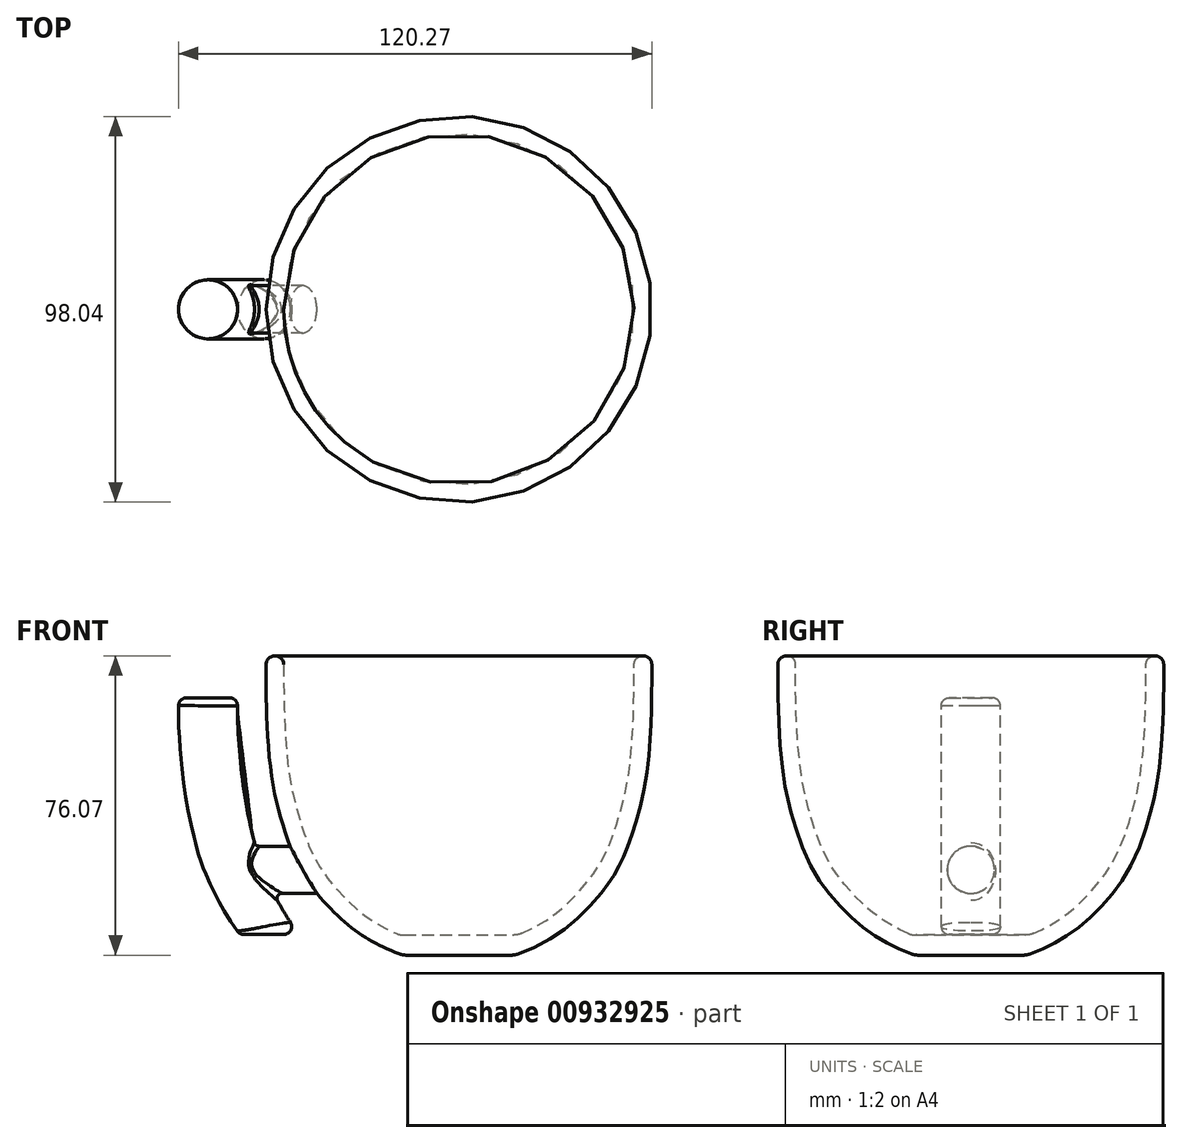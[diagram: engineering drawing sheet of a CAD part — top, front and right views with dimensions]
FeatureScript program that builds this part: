
annotation { "Feature Type Name" : "Feature", "Feature Type Description" : "" }
export const myFeature = defineFeature(function(context is Context, id is Id, definition is map)
    precondition{}
    {
        {
            var Q0;
            Q0=qCreatedBy(makeId("Front.planeOp"),FACE);
            var sketch = newSketch(context, id + "F0", { "sketchPlane" : qUnion([Q0])});
            skLineSegment(sketch, "E0", {"start": v(0, 78.82) * mm, "end": v(-49, 78.82) * mm});
            skLineSegment(sketch, "E1", {"start": v(0, 0) * mm, "end": v(0, 78.82) * mm});
            skFitSpline(sketch, "E2", {"points": [v(-49, 78.82) * mm, v(-49, 71.2) * mm, v(-47.95, 50.94) * mm, v(-44.24, 34.32) * mm, v(-38.54, 21.8) * mm, v(-27.37, 9.77) * mm, v(-17.3, 3.96) * mm, v(0, 0) * mm], "startDerivative": vector(-0.53, -120.05) * mm, "endDerivative": vector(126.32, 0) * mm});
            skSolve(sketch);
        }
        {
            var Q0;
            Q0=qSketchRegion(id+"F0",true);
            var Q1;
            Q1=sQuery(id+"F0.wireOp",EDGE,"E1");
            revolve(context, id + "F1", {"surfaceOperationType" : NewSurfaceOperationType.NEW, "entities" : qUnion([Q0]), "axis" : qUnion([Q1]), "revolveType" : RevolveType.FULL});
        }
        {
            var Q0;
            Q0=makeQuery(id+"F1.opRevolve","SWEPT_FACE",FACE,{"disambiguationData":[OSD([sQuery(id+"F0.wireOp",EDGE,"E0")])]});
            shell(context, id + "F2", {"entities" : qUnion([Q0]), "thickness" : 4.5 * mm});
        }
        {
            var Q0;
            Q0=makeQuery(id+"F1.opRevolve","SWEPT_EDGE",EDGE,{"disambiguationData":[OSD([sQuery(id+"F0.wireOp",EDGE,"E0"),sQuery(id+"F0.wireOp",EDGE,"E2")])]});
            var Q1;
            Q1=makeQuery(id+"F2.opShell","OFFSET_EDGE",EDGE,{"disambiguationData":[OSD([sQuery(id+"F0.wireOp",EDGE,"E0"),sQuery(id+"F0.wireOp",EDGE,"E2")])]});
            fillet(context, id + "F3", {"entities" : qUnion([Q0, Q1]), "radius" : 2.25 * mm, "tangentPropagation" : true, "defaultsChanged" : true, "vertexSettings" : [], "allowEdgeOverflow" : false});
        }
        {
            var Q0;
            Q0=qCreatedBy(makeId("Front.planeOp"),FACE);
            var sketch = newSketch(context, id + "F4", { "sketchPlane" : qUnion([Q0])});
            skLineSegment(sketch, "E3", {"start": v(-41.77, 30.38) * mm, "end": v(-53.43, 30.38) * mm});
            skLineSegment(sketch, "E4", {"start": v(-49.23, 20.12) * mm, "end": v(-36.53, 20.12) * mm});
            skLineSegment(sketch, "E5", {"start": v(-36.53, 20.12) * mm, "end": v(-41.77, 30.38) * mm});
            skFitSpline(sketch, "E6", {"points": [v(-42.03, 8) * mm, v(-47.44, 16.94) * mm, v(-49.23, 20.12) * mm, v(-51.33, 24.44) * mm, v(-53.43, 30.38) * mm, v(-55.23, 38.72) * mm, v(-56.67, 49.18) * mm, v(-57.32, 61.86) * mm, v(-57.58, 68.13) * mm, v(-57.6, 68.09) * mm], "startDerivative": vector(-47.1, 69.03) * mm, "endDerivative": vector(-6.03, -13.35) * mm});
            skLineSegment(sketch, "E7", {"start": v(-57.58, 68.13) * mm, "end": v(-69.83, 68.13) * mm});
            skFitSpline(sketch, "E8", {"points": [v(-69.83, 68.13) * mm, v(-69.83, 61.07) * mm, v(-69.06, 51.29) * mm, v(-67.63, 40.46) * mm, v(-65.54, 31.18) * mm, v(-63.64, 25) * mm, v(-58.64, 14.66) * mm, v(-54.3, 8) * mm], "startDerivative": vector(-1.12, -53.42) * mm, "endDerivative": vector(31.44, -44.67) * mm});
            skLineSegment(sketch, "E9", {"start": v(-54.3, 8) * mm, "end": v(-42.03, 8) * mm});
            skSolve(sketch);
        }
        {
            var Q0;
            Q0=qCreatedBy(makeId("Right.planeOp"),FACE);
            cPlane(context, id + "F5", {"entities" : qUnion([Q0]), "cplaneType" : CPlaneType.OFFSET, "offset" : 55 * mm, "oppositeDirection" : true, "width" : 150 * mm, "height" : 150 * mm});
        }
        {
            var Q0;
            Q0=qCreatedBy(id+"F5.planeOp",FACE);
            var sketch = newSketch(context, id + "F6", { "sketchPlane" : qUnion([Q0])});
            skPoint(sketch, "E10.middle", {"position": v(0, 24.44) * mm});
            skCircle(sketch, "E11", {"center": v(0, 24.44) * mm, "radius": 6 * mm});
            skSolve(sketch);
        }
        {
            var Q0;
            Q0=qSketchRegion(id+"F6",true);
            extrude(context, id + "F7", {"entities" : qUnion([Q0]), "operationType" : NewBodyOperationType.ADD, "endBound" : BoundingType.UP_TO_NEXT, "depth" : 25 * mm, "offsetDistance" : 25 * mm});
        }
        {
            var Q0;
            Q0=qCreatedBy(makeId("Top.planeOp"),FACE);
            cPlane(context, id + "F8", {"entities" : qUnion([Q0]), "cplaneType" : CPlaneType.OFFSET, "offset" : 8 * mm, "width" : 150 * mm, "height" : 150 * mm});
        }
        {
            var Q0;
            Q0=qCreatedBy(id+"F8.planeOp",FACE);
            var sketch = newSketch(context, id + "F9", { "sketchPlane" : qUnion([Q0])});
            skPoint(sketch, "E12.middle", {"position": v(-48.17, 0) * mm});
            skCircle(sketch, "E13", {"center": v(-48.17, 0) * mm, "radius": 7.5 * mm});
            skSolve(sketch);
        }
        {
            var Q0;
            Q0=qSketchRegion(id+"F9",true);
            var Q1;
            Q1=sQuery(id+"F4.wireOp",EDGE,"E8");
            sweep(context, id + "F10", {"operationType" : NewBodyOperationType.ADD, "profiles" : qUnion([Q0]), "path" : qUnion([Q1]), "keepProfileOrientation" : true});
        }
        {
            var Q0;
            Q0=makeQuery(id+"F10.opSweep","CAP_FACE",FACE,{"disambiguationData":[OSD([sQuery(id+"F4.wireOp",VERTEX,"E8.start"),sQuery(id+"F9.wireOp",EDGE,"E12.bottom"),sQuery(id+"F9.wireOp",EDGE,"E12.top"),sQuery(id+"F9.wireOp",EDGE,"E12.left"),sQuery(id+"F9.wireOp",EDGE,"E12.right")])],"isStart":false});
            var Q1;
            Q1=makeQuery(id+"F10.opSweep","CAP_FACE",FACE,{"disambiguationData":[OSD([sQuery(id+"F4.wireOp",VERTEX,"E8.end"),sQuery(id+"F9.wireOp",EDGE,"E12.bottom"),sQuery(id+"F9.wireOp",EDGE,"E12.top"),sQuery(id+"F9.wireOp",EDGE,"E12.left"),sQuery(id+"F9.wireOp",EDGE,"E12.right")])],"isStart":true});
            fillet(context, id + "F11", {"entities" : qUnion([Q0, Q1]), "radius" : 2 * mm, "tangentPropagation" : true, "allowEdgeOverflow" : false});
        }
        {
            var Q0;
            Q0=qCreatedBy(makeId("Front.planeOp"),FACE);
            var sketch = newSketch(context, id + "F12", { "sketchPlane" : qUnion([Q0])});
            skLineSegment(sketch, "E14", {"start": v(0, 1.35) * mm, "end": v(0, 7.85) * mm});
            skLineSegment(sketch, "E15", {"start": v(0, 7.85) * mm, "end": v(-21, 7.85) * mm});
            skLineSegment(sketch, "E16", {"start": v(-21, 7.85) * mm, "end": v(0, 1.35) * mm});
            skSolve(sketch);
        }
        {
            var Q0;
            Q0=qSketchRegion(id+"F12",true);
            var Q1;
            Q1=sQuery(id+"F12.wireOp",EDGE,"E14");
            revolve(context, id + "F13", {"operationType" : NewBodyOperationType.ADD, "surfaceOperationType" : NewSurfaceOperationType.NEW, "entities" : qUnion([Q0]), "axis" : qUnion([Q1]), "revolveType" : RevolveType.FULL});
        }
        {
            var Q0;
            Q0=qCreatedBy(makeId("Front.planeOp"),FACE);
            var sketch = newSketch(context, id + "F14", { "sketchPlane" : qUnion([Q0])});
            skLineSegment(sketch, "E17.bottom", {"start": v(20, 0) * mm, "end": v(-20, 0) * mm});
            skLineSegment(sketch, "E17.top", {"start": v(20, 2.75) * mm, "end": v(-20, 2.75) * mm});
            skLineSegment(sketch, "E17.left", {"start": v(20, 0) * mm, "end": v(20, 2.75) * mm});
            skLineSegment(sketch, "E17.right", {"start": v(-20, 0) * mm, "end": v(-20, 2.75) * mm});
            skSolve(sketch);
        }
        {
            var Q0;
            Q0=qSketchRegion(id+"F14",true);
            extrude(context, id + "F15", {"entities" : qUnion([Q0]), "operationType" : NewBodyOperationType.REMOVE, "oppositeDirection" : true, "depth" : 40 * mm, "offsetDistance" : 25 * mm, "symmetric" : true});
        }
        {
            var Q0;
            Q0=makeQuery(id+"F15.boolean.opBoolean","INTERSECT",EDGE,{"derivedFrom":[makeQuery(id+"F1.opRevolve","SWEPT_FACE",FACE,{"disambiguationData":[OSD([sQuery(id+"F0.wireOp",EDGE,"E2")])]}),makeQuery(id+"F15.opExtrude","SWEPT_FACE",FACE,{"disambiguationData":[OSD([sQuery(id+"F14.wireOp",EDGE,"E17.top")])]})]});
            var Q1;
            Q1=makeQuery(id+"F13.boolean.opBoolean","INTERSECT",EDGE,{"derivedFrom":[makeQuery(id+"F2.opShell","OFFSET_FACE",FACE,{"disambiguationData":[OSD([sQuery(id+"F0.wireOp",EDGE,"E2")])]}),makeQuery(id+"F13.opRevolve","SWEPT_FACE",FACE,{"disambiguationData":[OSD([sQuery(id+"F12.wireOp",EDGE,"E15")])]})]});
            fillet(context, id + "F16", {"entities" : qUnion([Q0, Q1]), "tangentPropagation" : true, "radius" : 5 * mm, "defaultsChanged" : false, "vertexSettings" : [], "allowEdgeOverflow" : false});
        }
        {
            var Q0;
            Q0=makeQuery(id+"F7.opExtrude","CAP_EDGE",EDGE,{"disambiguationData":[OSD([sQuery(id+"F6.wireOp",EDGE,"E11")])],"isStart":false});
            var Q1;
            Q1=makeQuery(id+"F10.boolean.opBoolean","INTERSECT",EDGE,{"derivedFrom":[makeQuery(id+"F7.opExtrude","SWEPT_FACE",FACE,{"disambiguationData":[OSD([sQuery(id+"F6.wireOp",EDGE,"E11")])]}),makeQuery(id+"F10.opSweep","SWEPT_FACE",FACE,{"disambiguationData":[OSD([sQuery(id+"F4.wireOp",EDGE,"E8"),sQuery(id+"F9.wireOp",EDGE,"E13")])]})]});
            fillet(context, id + "F17", {"entities" : qUnion([Q0, Q1]), "tangentPropagation" : true, "radius" : 1.25 * mm, "defaultsChanged" : true, "vertexSettings" : [], "allowEdgeOverflow" : false});
        }
    });
